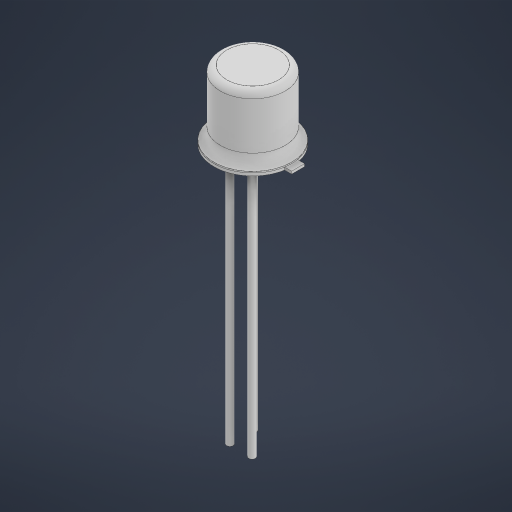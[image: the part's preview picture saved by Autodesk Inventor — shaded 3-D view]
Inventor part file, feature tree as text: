
AUTODESK INVENTOR PART (.ipt)
format: ipt  version: 2024 (Build 280153000, 153)  size: 234,496 bytes
history: native  units: in
note: dims shown in document units (in); Inventor stores cm internally (conversion verified against a paired STEP export)
features: extrude x4, sketch x4, fillet x2
ambient origin geometry x8: Origin, YZ Plane, XZ Plane, XY Plane, X Axis, Y Axis, Z Axis, Center Point
bodies: Solid1 (feature_tree)
feature tree (10):
  extrude  "Extrusion1"  Depth=0.0197in
  extrude  "Extrusion2"  Depth=0.0197in
  extrude  "Extrusion3"  Depth=0.0079in TaperAngle=0.0deg
  fillet  "Fillet1"  Radius=0.1969in
  fillet  "Fillet2"  Radius=0.1969in
  extrude  "Extrusion4"  Depth=0.0394in
  sketch  "Sketch1"  dims[d0=0.2362in d1=0.0197in]
  sketch  "Sketch2"  dims[d2=0.0197in d3=0.0197in]
  sketch  "Sketch3"  dims[d4=0.0079in d5=0.0in d6=0.0039in d7=0.0in d8=0.1969in d9=0.1969in d10=0.0in]
  sketch  "Sketch4"  dims[d11=0.0197in d12=0.0394in d13=0.0984in d14=0.0197in d16=0.0197in d17=0.0197in d18=0.0197in d19=0.7874in d20=0.0in]
